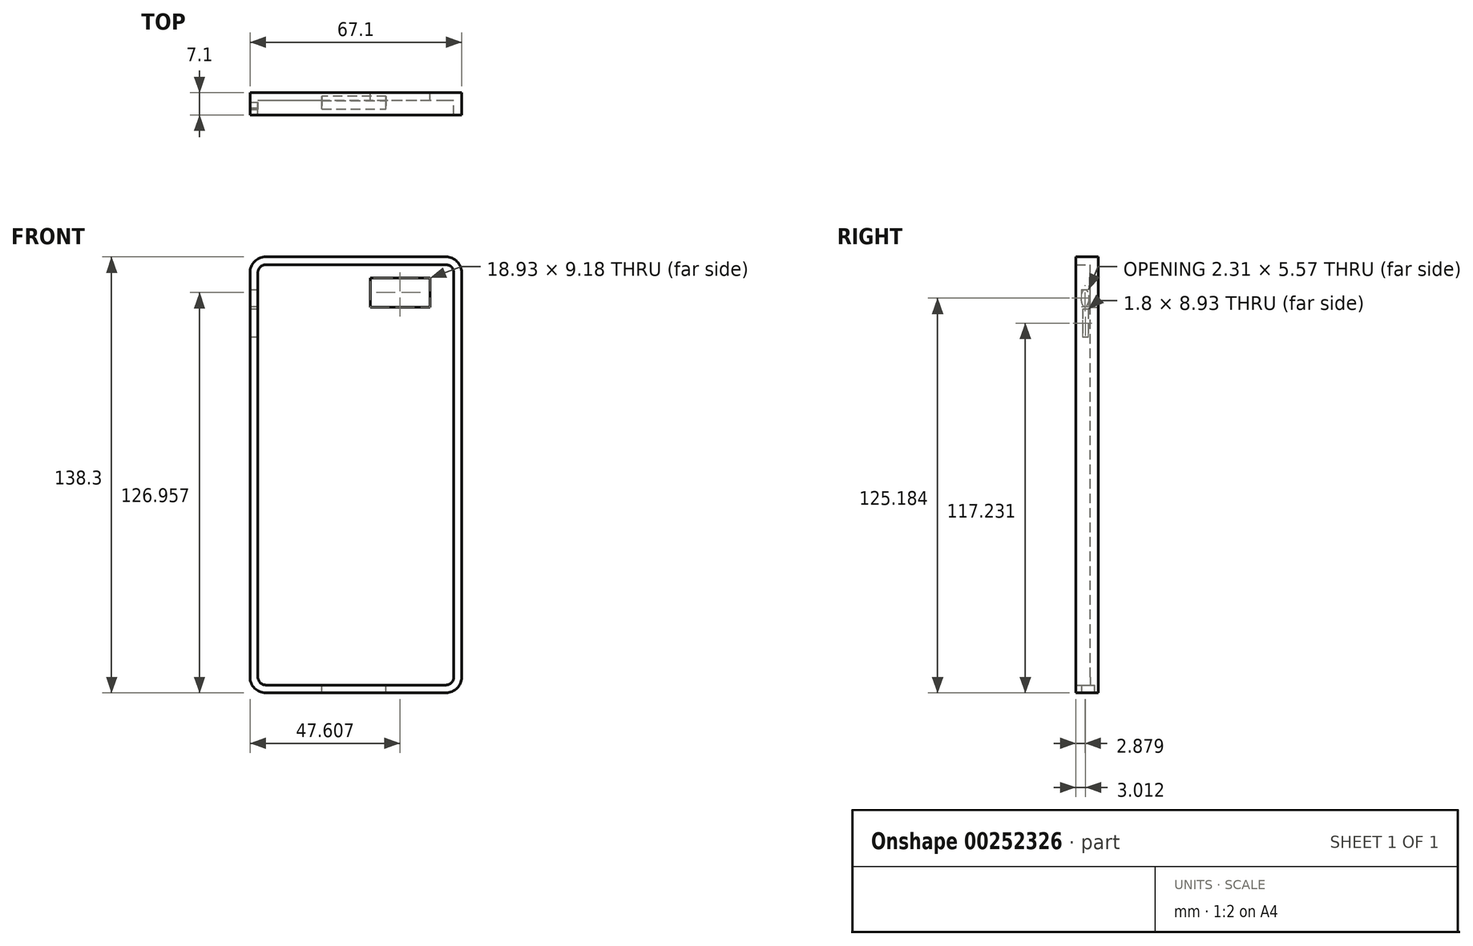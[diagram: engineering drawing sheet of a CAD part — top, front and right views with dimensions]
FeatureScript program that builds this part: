
annotation { "Feature Type Name" : "Feature", "Feature Type Description" : "" }
export const myFeature = defineFeature(function(context is Context, id is Id, definition is map)
    precondition{}
    {
        {
            var Q0;
            Q0=qCreatedBy(makeId("Front.planeOp"),FACE);
            var sketch = newSketch(context, id + "F0", { "sketchPlane" : qUnion([Q0])});
            skLineSegment(sketch, "E0.bottom", {"start": v(33.55, -69.15) * mm, "end": v(-33.55, -69.15) * mm});
            skLineSegment(sketch, "E0.top", {"start": v(33.55, 69.15) * mm, "end": v(-33.55, 69.15) * mm});
            skLineSegment(sketch, "E0.left", {"start": v(33.55, -69.15) * mm, "end": v(33.55, 69.15) * mm});
            skLineSegment(sketch, "E0.right", {"start": v(-33.55, -69.15) * mm, "end": v(-33.55, 69.15) * mm});
            skPoint(sketch, "E0.middle", {"position": v(0, 0) * mm});
            skSolve(sketch);
        }
        {
            var Q0;
            Q0=makeQuery(id+"F0.imprint","IMPRINT",FACE,{"disambiguationData":[TD([[makeQuery(id+"F0.imprint","IMPRINT",EDGE,{"derivedFrom":sQuery(id+"F0.wireOp",EDGE,"E0.bottom")}),-1.0]])]});
            extrude(context, id + "F1", {"entities" : qUnion([Q0]), "endBound" : BoundingType.SYMMETRIC, "depth" : 7.1 * mm});
        }
        {
            var Q0;
            Q0=makeQuery(id+"F1.opExtrude","SWEPT_EDGE",EDGE,{"disambiguationData":[OSD([sQuery(id+"F0.wireOp",EDGE,"E0.top"),sQuery(id+"F0.wireOp",EDGE,"E0.right")])]});
            var Q1;
            Q1=makeQuery(id+"F1.opExtrude","SWEPT_EDGE",EDGE,{"disambiguationData":[OSD([sQuery(id+"F0.wireOp",EDGE,"E0.top"),sQuery(id+"F0.wireOp",EDGE,"E0.left")])]});
            var Q2;
            Q2=makeQuery(id+"F1.opExtrude","SWEPT_EDGE",EDGE,{"disambiguationData":[OSD([sQuery(id+"F0.wireOp",EDGE,"E0.bottom"),sQuery(id+"F0.wireOp",EDGE,"E0.right")])]});
            var Q3;
            Q3=makeQuery(id+"F1.opExtrude","SWEPT_EDGE",EDGE,{"disambiguationData":[OSD([sQuery(id+"F0.wireOp",EDGE,"E0.bottom"),sQuery(id+"F0.wireOp",EDGE,"E0.left")])]});
            fillet(context, id + "F2", {"entities" : qUnion([Q0, Q1, Q2, Q3]), "radius" : 5 * mm, "tangentPropagation" : true, "allowEdgeOverflow" : false});
        }
        {
            var Q0;
            Q0=makeQuery(id+"F1.opExtrude","CAP_FACE",FACE,{"disambiguationData":[OSD([sQuery(id+"F0.wireOp",EDGE,"E0.bottom"),sQuery(id+"F0.wireOp",EDGE,"E0.top"),sQuery(id+"F0.wireOp",EDGE,"E0.left"),sQuery(id+"F0.wireOp",EDGE,"E0.right")])],"isStart":false});
            shell(context, id + "F3", {"entities" : qUnion([Q0]), "thickness" : 2.5 * mm});
        }
        {
            var Q0;
            Q0=qCreatedBy(makeId("Front.planeOp"),FACE);
            var sketch = newSketch(context, id + "F4", { "sketchPlane" : qUnion([Q0])});
            skLineSegment(sketch, "E1.bottom", {"start": v(4.6, 62.4) * mm, "end": v(23.52, 62.4) * mm});
            skLineSegment(sketch, "E1.top", {"start": v(4.6, 53.22) * mm, "end": v(23.52, 53.22) * mm});
            skLineSegment(sketch, "E1.left", {"start": v(4.6, 62.4) * mm, "end": v(4.6, 53.22) * mm});
            skLineSegment(sketch, "E1.right", {"start": v(23.52, 62.4) * mm, "end": v(23.52, 53.22) * mm});
            skSolve(sketch);
        }
        {
            var Q0;
            Q0=makeQuery(id+"F4.imprint","IMPRINT",FACE,{"disambiguationData":[TD([[makeQuery(id+"F4.imprint","IMPRINT",EDGE,{"derivedFrom":sQuery(id+"F4.wireOp",EDGE,"E1.bottom")}),-1.0]])]});
            extrude(context, id + "F5", {"entities" : qUnion([Q0]), "operationType" : NewBodyOperationType.REMOVE, "endBound" : BoundingType.SYMMETRIC, "depth" : 25 * mm});
        }
        {
            var Q0;
            Q0=makeQuery(id+"F1.opExtrude","SWEPT_FACE",FACE,{"disambiguationData":[OSD([sQuery(id+"F0.wireOp",EDGE,"E0.bottom")])]});
            var sketch = newSketch(context, id + "F6", { "sketchPlane" : qUnion([Q0])});
            skSolve(sketch);
        }
        {
            var Q0;
            {var subQ0=sQuery(id+"F0.wireOp",EDGE,"E0.bottom");Q0=makeQuery(id+"F6.imprint","IMPRINT",FACE,{"disambiguationData":[TD([[makeQuery(id+"F6.imprint","IMPRINT",EDGE,{"derivedFrom":makeQuery(id+"F1.opExtrude","CAP_EDGE",EDGE,{"disambiguationData":[OSD([subQ0])],"isStart":true})}),-1.0]])]});}
            var sketch = newSketch(context, id + "F7", { "sketchPlane" : qUnion([Q0])});
            skLineSegment(sketch, "E2.bottom", {"start": v(-10.77, 1.7) * mm, "end": v(9.58, 1.7) * mm});
            skLineSegment(sketch, "E2.top", {"start": v(-10.77, -2.38) * mm, "end": v(9.58, -2.38) * mm});
            skLineSegment(sketch, "E2.left", {"start": v(-10.77, 1.7) * mm, "end": v(-10.77, -2.38) * mm});
            skLineSegment(sketch, "E2.right", {"start": v(9.58, 1.7) * mm, "end": v(9.58, -2.38) * mm});
            skSolve(sketch);
        }
        {
            var Q0;
            Q0 = qSketchRegion(id + "F7", true);
            extrude(context, id + "F8", {"entities" : qUnion([Q0]), "operationType" : NewBodyOperationType.REMOVE, "endBound" : BoundingType.SYMMETRIC, "depth" : 4.97 * mm});
        }
        {
            var Q0;
            Q0=makeQuery(id+"F1.opExtrude","SWEPT_FACE",FACE,{"disambiguationData":[OSD([sQuery(id+"F0.wireOp",EDGE,"E0.right")])]});
            var sketch = newSketch(context, id + "F9", { "sketchPlane" : qUnion([Q0])});
            skEllipse(sketch, "E3", {"center": v(0.67, 56.03) * mm, "majorRadius": 2.78 * mm, "minorRadius": 1.15 * mm, "majorAxis": v(0, -1)});
            skLineSegment(sketch, "E4.bottom", {"start": v(-0.36, 52.55) * mm, "end": v(1.44, 52.55) * mm});
            skLineSegment(sketch, "E4.top", {"start": v(-0.36, 43.62) * mm, "end": v(1.44, 43.62) * mm});
            skLineSegment(sketch, "E4.left", {"start": v(-0.36, 52.55) * mm, "end": v(-0.36, 43.62) * mm});
            skLineSegment(sketch, "E4.right", {"start": v(1.44, 52.55) * mm, "end": v(1.44, 43.62) * mm});
            skSolve(sketch);
        }
        {
            var Q0;
            Q0=makeQuery(id+"F9.imprint","IMPRINT",FACE,{"disambiguationData":[TD([[makeQuery(id+"F9.imprint","IMPRINT",EDGE,{"derivedFrom":sQuery(id+"F9.wireOp",EDGE,"E3")}),1.0]])]});
            var Q1;
            Q1=makeQuery(id+"F9.imprint","IMPRINT",FACE,{"disambiguationData":[TD([[makeQuery(id+"F9.imprint","IMPRINT",EDGE,{"derivedFrom":sQuery(id+"F9.wireOp",EDGE,"E4.bottom")}),-1.0]])]});
            extrude(context, id + "F10", {"entities" : qUnion([Q0, Q1]), "operationType" : NewBodyOperationType.REMOVE, "oppositeDirection" : true, "depth" : 25 * mm});
        }
    });
